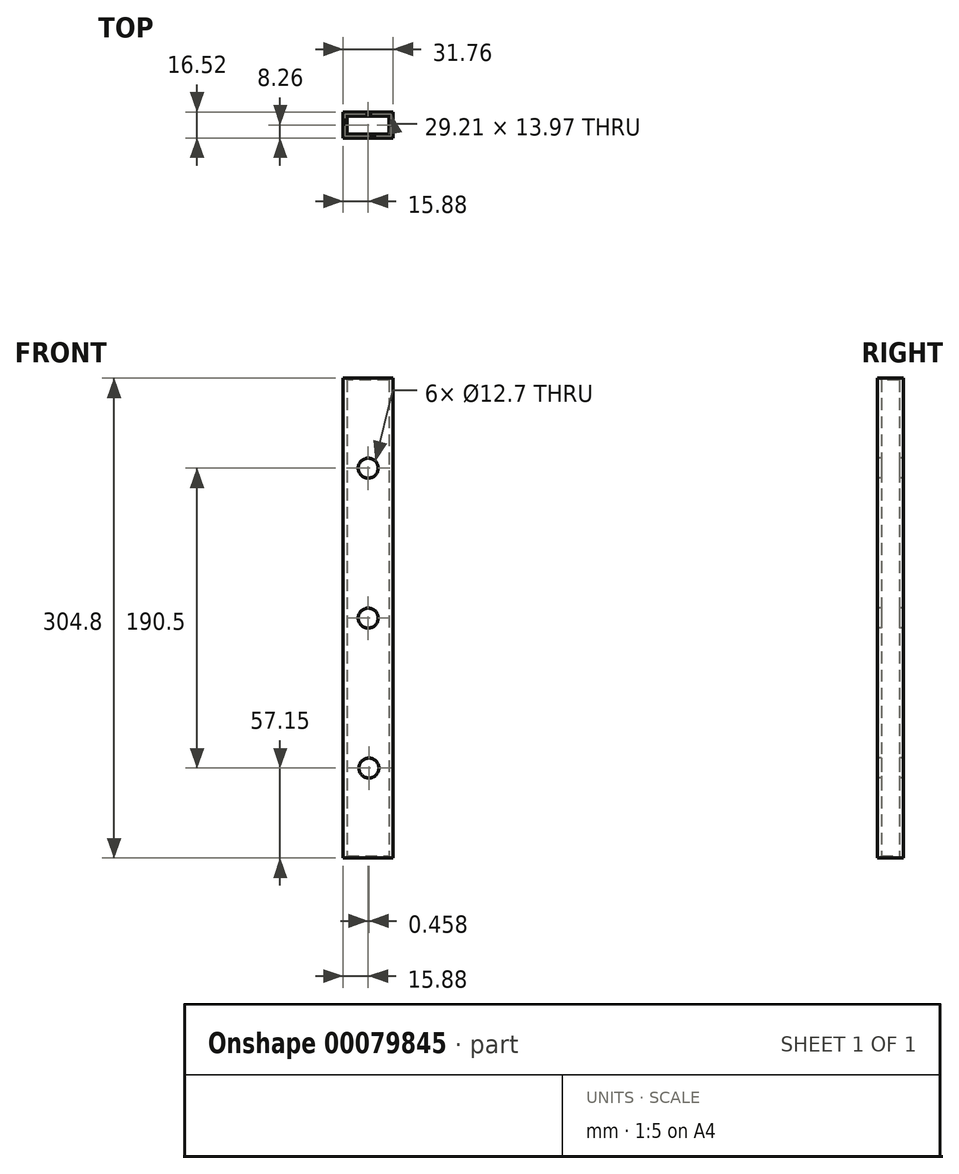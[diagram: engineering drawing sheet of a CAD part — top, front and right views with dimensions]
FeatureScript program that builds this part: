
annotation { "Feature Type Name" : "Feature", "Feature Type Description" : "" }
export const myFeature = defineFeature(function(context is Context, id is Id, definition is map)
    precondition{}
    {
        {
            var Q0;
            Q0=qCreatedBy(makeId("Top.planeOp"),FACE);
            var sketch = newSketch(context, id + "F0", { "sketchPlane" : qUnion([Q0])});
            skLineSegment(sketch, "E0.bottom", {"start": v(-15.88, -8.26) * mm, "end": v(15.88, -8.26) * mm});
            skLineSegment(sketch, "E0.top", {"start": v(-15.88, 8.26) * mm, "end": v(15.88, 8.26) * mm});
            skLineSegment(sketch, "E0.left", {"start": v(-15.88, -8.26) * mm, "end": v(-15.88, 8.26) * mm});
            skLineSegment(sketch, "E0.right", {"start": v(15.88, -8.26) * mm, "end": v(15.88, 8.26) * mm});
            skPoint(sketch, "E0.middle", {"position": v(0, 0) * mm});
            skLineSegment(sketch, "E1.bottom", {"start": v(-13.33, 5.72) * mm, "end": v(13.33, 5.72) * mm});
            skLineSegment(sketch, "E1.top", {"start": v(-13.33, -5.72) * mm, "end": v(13.33, -5.72) * mm});
            skLineSegment(sketch, "E1.left", {"start": v(-13.33, 5.72) * mm, "end": v(-13.33, -5.72) * mm});
            skLineSegment(sketch, "E1.right", {"start": v(13.33, 5.72) * mm, "end": v(13.33, -5.72) * mm});
            skSolve(sketch);
        }
        {
            var Q0;
            Q0=makeQuery(id+"F0.imprint","IMPRINT",FACE,{"disambiguationData":[TD([[makeQuery(id+"F0.imprint","IMPRINT",EDGE,{"derivedFrom":sQuery(id+"F0.wireOp",EDGE,"E0.bottom")}),1.0]])]});
            extrude(context, id + "F1", {"entities" : qUnion([Q0]), "depth" : 304.8 * mm});
        }
        {
            var Q0;
            Q0=makeQuery(id+"F1.opExtrude","CAP_EDGE",EDGE,{"disambiguationData":[OSD([sQuery(id+"F0.wireOp",EDGE,"E1.bottom")])],"isStart":false});
            var Q1;
            Q1=makeQuery(id+"F1.opExtrude","CAP_EDGE",EDGE,{"disambiguationData":[OSD([sQuery(id+"F0.wireOp",EDGE,"E1.left")])],"isStart":false});
            var Q2;
            Q2=makeQuery(id+"F1.opExtrude","CAP_EDGE",EDGE,{"disambiguationData":[OSD([sQuery(id+"F0.wireOp",EDGE,"E1.top")])],"isStart":false});
            var Q3;
            Q3=makeQuery(id+"F1.opExtrude","CAP_EDGE",EDGE,{"disambiguationData":[OSD([sQuery(id+"F0.wireOp",EDGE,"E1.right")])],"isStart":false});
            chamfer(context, id + "F2", {"entities" : qUnion([Q0, Q1, Q2, Q3]), "width" : 1.27 * mm, "tangentPropagation" : true});
        }
        {
            var Q0;
            Q0=makeQuery(id+"F1.opExtrude","CAP_EDGE",EDGE,{"disambiguationData":[OSD([sQuery(id+"F0.wireOp",EDGE,"E1.right")])],"isStart":true});
            var Q1;
            Q1=makeQuery(id+"F1.opExtrude","CAP_EDGE",EDGE,{"disambiguationData":[OSD([sQuery(id+"F0.wireOp",EDGE,"E1.bottom")])],"isStart":true});
            var Q2;
            Q2=makeQuery(id+"F1.opExtrude","CAP_EDGE",EDGE,{"disambiguationData":[OSD([sQuery(id+"F0.wireOp",EDGE,"E1.left")])],"isStart":true});
            var Q3;
            Q3=makeQuery(id+"F1.opExtrude","CAP_EDGE",EDGE,{"disambiguationData":[OSD([sQuery(id+"F0.wireOp",EDGE,"E1.top")])],"isStart":true});
            chamfer(context, id + "F3", {"entities" : qUnion([Q0, Q1, Q2, Q3]), "width" : 1.27 * mm, "tangentPropagation" : true});
        }
        {
            var Q0;
            Q0=makeQuery(id+"F1.opExtrude","SWEPT_FACE",FACE,{"disambiguationData":[OSD([sQuery(id+"F0.wireOp",EDGE,"E0.bottom")])]});
            var sketch = newSketch(context, id + "F4", { "sketchPlane" : qUnion([Q0])});
            skCircle(sketch, "E2", {"center": v(0, 247.65) * mm, "radius": 6.35 * mm});
            skCircle(sketch, "E3", {"center": v(0, 152.4) * mm, "radius": 6.35 * mm});
            skCircle(sketch, "E4", {"center": v(0, 152.4) * mm, "radius": 6.2 * mm});
            skCircle(sketch, "E5", {"center": v(0, 247.65) * mm, "radius": 6.4 * mm});
            skCircle(sketch, "E6", {"center": v(0.46, 57.15) * mm, "radius": 6.4 * mm});
            skLineSegment(sketch, "E7", {"start": v(-15.88, 152.4) * mm, "end": v(143.34, 152.4) * mm, "construction": true});
            skLineSegment(sketch, "E8", {"start": v(-15.88, 152.4) * mm, "end": v(-144.72, 152.4) * mm, "construction": true});
            skCircle(sketch, "E9", {"center": v(0.46, 57.15) * mm, "radius": 6.35 * mm});
            skSolve(sketch);
        }
        {
            var Q0;
            Q0=sQuery(id+"F4.wireOp",VERTEX,"E4.center");
            var Q1;
            Q1=sQuery(id+"F4.wireOp",VERTEX,"E5.center");
            var Q2;
            Q2=sQuery(id+"F4.wireOp",VERTEX,"E9.center");
            var Q3;
            Q3=makeQuery(id+"F1.opExtrude","SWEPT_BODY",BODY,{"disambiguationData":[OSD([sQuery(id+"F0.wireOp",EDGE,"E0.bottom"),sQuery(id+"F0.wireOp",EDGE,"E0.top"),sQuery(id+"F0.wireOp",EDGE,"E0.left"),sQuery(id+"F0.wireOp",EDGE,"E0.right"),sQuery(id+"F0.wireOp",EDGE,"E1.bottom"),sQuery(id+"F0.wireOp",EDGE,"E1.top"),sQuery(id+"F0.wireOp",EDGE,"E1.left"),sQuery(id+"F0.wireOp",EDGE,"E1.right")])]});
            hole(context, id + "F5", {"style" : HoleStyle.SIMPLE, "endStyle" : HoleEndStyle.BLIND, "holeDiameter" : 12.7 * mm, "holeDepth" : 25.4 * mm, "startFromSketch" : true, "locations" : qUnion([Q0, Q1, Q2]), "scope" : qUnion([Q3])});
        }
    });
